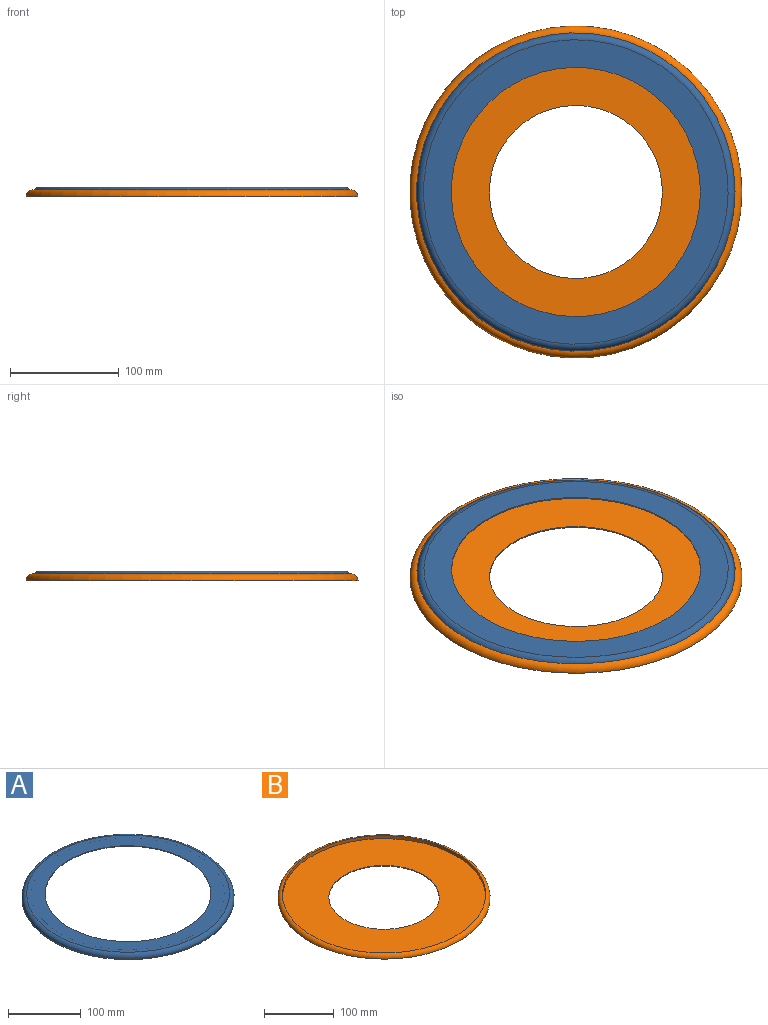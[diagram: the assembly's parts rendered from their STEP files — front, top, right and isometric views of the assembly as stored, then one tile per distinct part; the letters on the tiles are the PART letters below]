
ASSEMBLY  parts=2 mates=1
PART A: 7 faces, bbox 316.2x316.2x8 mm
  f0: cylinder r=133.35mm len=266.7mm, axis (0,0,-1), area 5865mm2, adj f3,f5
  f1: cylinder r=146.05mm len=292.1mm, axis (0,0,-1), area 1514.1mm2, adj f3,f6
  f2: plane 279.4x279.4mm, normal (0,0,1), area 20268.3mm2, adj f4,f6
  f3: plane 292.1x292.1mm, normal (0,0,-1), area 11147.6mm2, adj f0,f1
  f4: cylinder r=114.3mm len=228.6mm, axis (0,0,1), area 718.2mm2, adj f2,f5
  f5: plane 266.7x266.7mm, normal (0,0,-1), area 14821.2mm2, adj f0,f4
  f6: torus R=139.7mm, axis (0,0,1), area 9008.6mm2, adj f1,f2
PART B: 5 faces, bbox 329.9x329.9x6.4 mm
  f0: cylinder r=146.05mm len=292.1mm, axis (0,0,-1), area 4909.5mm2, adj f3,f4
  f1: plane 304.8x304.8mm, normal (0,0,-1), area 53172.6mm2, adj f2,f4
  f2: cylinder r=79.38mm len=158.75mm, axis (0,0,-1), area 498.7mm2, adj f1,f3
  f3: plane 292.1x292.1mm, normal (0,0,1), area 47218.8mm2, adj f0,f2
  f4: torus R=146.05mm, axis (0,0,1), area 9406.6mm2, adj f0,f1
PLACE A rot(axis=(0,0,1),112.5deg) t=(0,0,0)mm
PLACE B at identity
MATE revolute A.f4 <-> B.f0  axis (0,0,-1) through (0,0,1)mm
